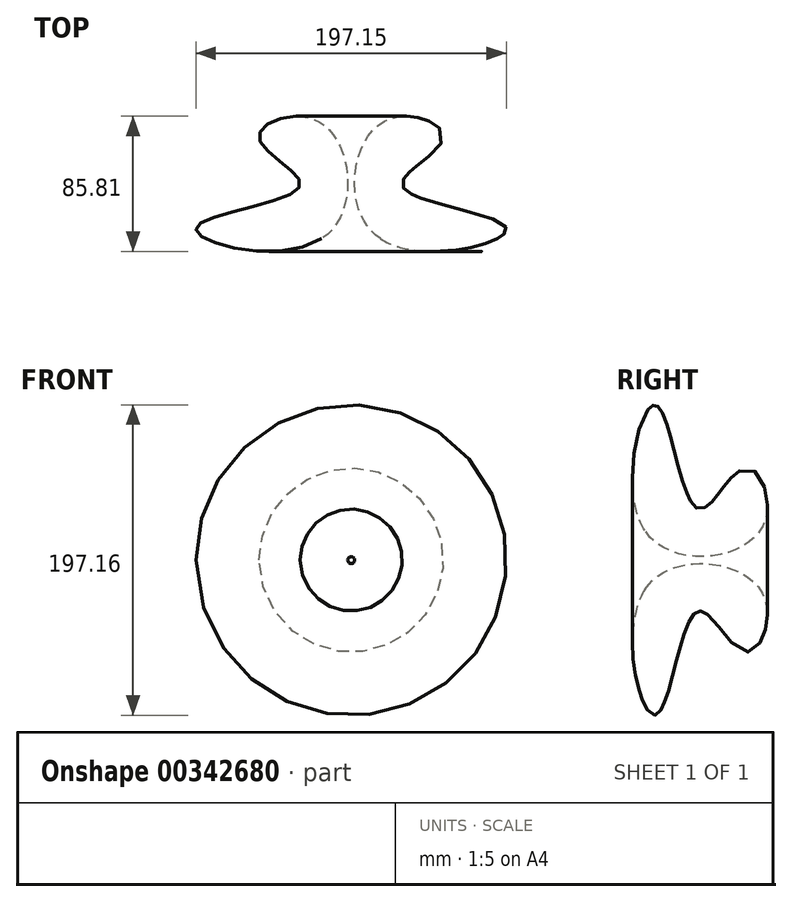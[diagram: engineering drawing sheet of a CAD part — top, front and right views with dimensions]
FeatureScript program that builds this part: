
annotation { "Feature Type Name" : "Feature", "Feature Type Description" : "" }
export const myFeature = defineFeature(function(context is Context, id is Id, definition is map)
    precondition{}
    {
        {
            var Q0;
            Q0=qCreatedBy(makeId("Top.planeOp"),FACE);
            var sketch = newSketch(context, id + "F0", { "sketchPlane" : qUnion([Q0])});
            skFitSpline(sketch, "E0", {"points": [v(-11.61, -33.55) * mm, v(-91.3, -26.45) * mm, v(-25.49, 0) * mm, v(-51.3, 30.33) * mm, v(-13.23, 40.65) * mm, v(-11.61, -33.55) * mm]});
            skLineSegment(sketch, "E1", {"start": v(7.1, 44.84) * mm, "end": v(7.1, -38.4) * mm});
            skSolve(sketch);
        }
        {
            var Q0;
            Q0 = qSketchRegion(id + "F0", true);
            var Q1;
            Q1=sQuery(id+"F0.wireOp",EDGE,"E1");
            revolve(context, id + "F1", {"entities" : qUnion([Q0]), "axis" : qUnion([Q1]), "revolveType" : RevolveType.FULL});
        }
    });
